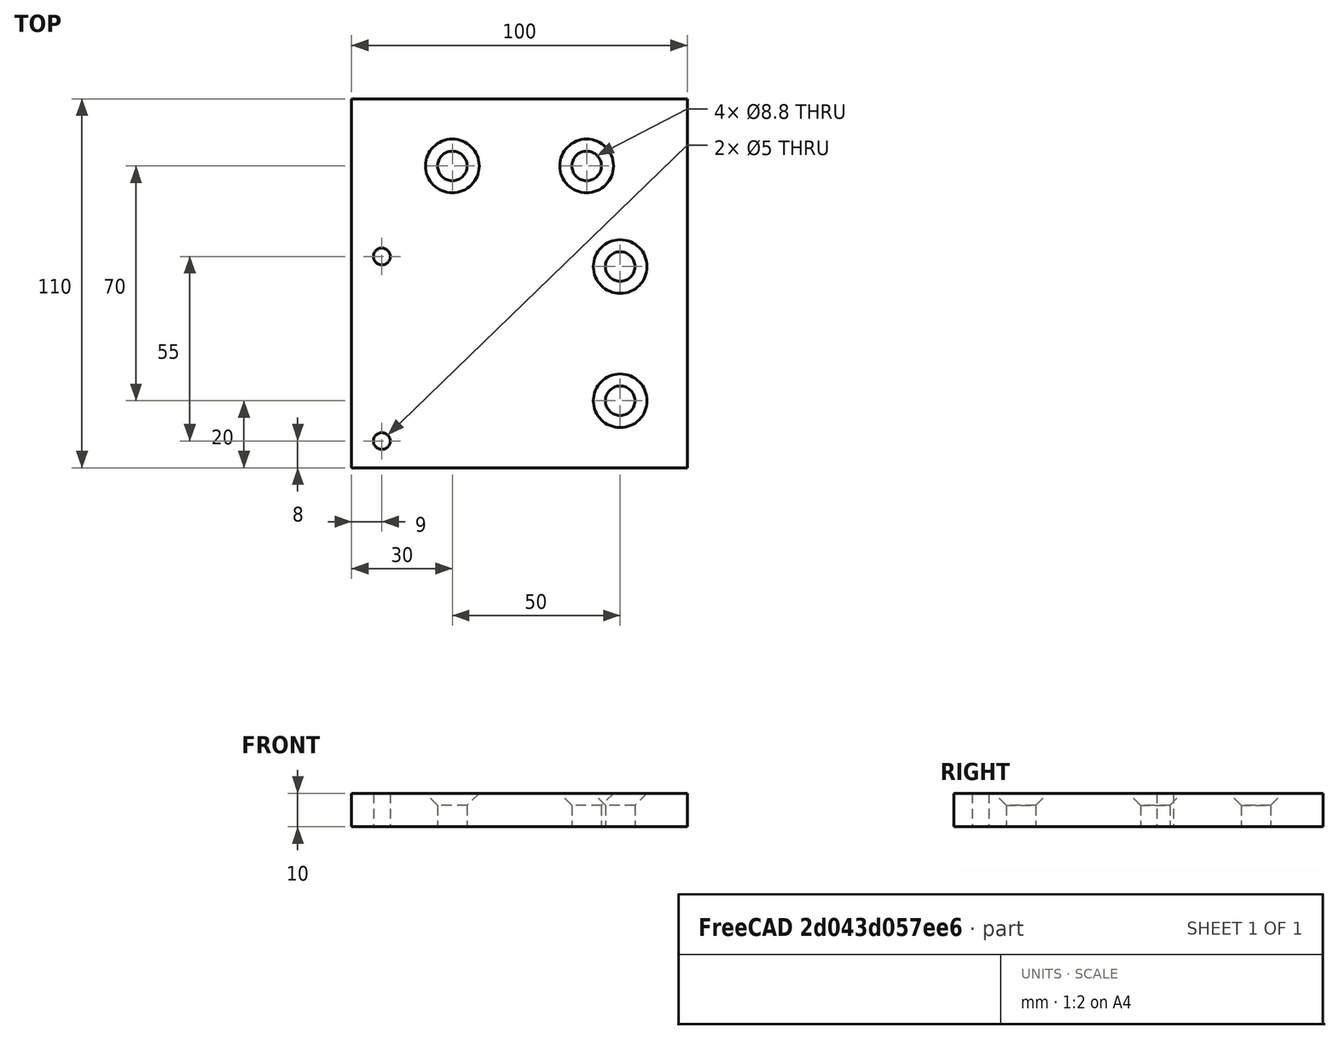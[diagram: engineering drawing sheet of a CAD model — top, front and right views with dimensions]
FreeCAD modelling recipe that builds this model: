
FCSTD DOCUMENT  (FreeCAD 0.17R13528 (Git))
Label: plate3
License: All rights reserved
LicenseURL: http://en.wikipedia.org/wiki/All_rights_reserved
objects: TechDraw::DrawViewDimension×17, Sketcher::SketchObject×4, PartDesign::Hole×3, PartDesign::LinearPattern×3, TechDraw::DrawProjGroupItem×3, PartDesign::Pad×1, PartDesign::Body×1, TechDraw::DrawSVGTemplate×1, TechDraw::DrawProjGroup×1, TechDraw::DrawViewAnnotation×1, TechDraw::DrawPage×1
note: 16 computed .brp shape members not serialized (recipe doc carries the construction recipe); baked Part::Feature solids carry a one-line shape summary decoded from their .brp

FEATURE [Sketcher::SketchObject] Sketch
  MapMode = 5
  Support = -> [XY_Plane]
  sketch-geometry (4):
    g0: LineSegment StartX=0 StartY=0 StartZ=0 EndX=100 EndY=0 EndZ=0
    g1: LineSegment StartX=100 StartY=0 StartZ=0 EndX=100 EndY=110 EndZ=0
    g2: LineSegment StartX=100 StartY=110 StartZ=0 EndX=0 EndY=110 EndZ=0
    g3: LineSegment StartX=0 StartY=110 StartZ=0 EndX=0 EndY=0 EndZ=0
  constraints (11):
    c: Coincident(g0,g1)
    c: Coincident(g1,g2)
    c: Coincident(g2,g3)
    c: Coincident(g3,g0)
    c: Horizontal(g0)
    c: Horizontal(g2)
    c: Vertical(g1)
    c: Vertical(g3)
    c: Coincident(g0,g-1)
    c: DistanceX(g0,g0) = 100
    c: DistanceY(g3,g3) = 110
FEATURE [PartDesign::Pad] Pad
  Length = 10
  Length2 = 100
  Profile = -> Sketch
  Type = 0
FEATURE [Sketcher::SketchObject] Sketch001
  MapMode = 5
  Placement = pos=(0,0,10) rot=(0,0,1;0rad)
  Support = -> [Pad]
  sketch-geometry (1):
    g0: Circle CenterX=9 CenterY=8 CenterZ=0 NormalX=0 NormalY=0 NormalZ=1 AngleXU=0 Radius=4.49838
  constraints (2):
    c: Distance(g0,g-1) = 8
    c: Distance(g0,g-2) = 9
FEATURE [PartDesign::Hole] Hole
  BaseFeature = -> Pad
  Depth = 25
  DepthType = 1
  Diameter = 5
  DrillPoint = 0
  DrillPointAngle = 118
  HoleCutCountersinkAngle = 90
  HoleCutDepth = 0
  HoleCutDiameter = 6
  HoleCutType = 0
  ModelActualThread = false
  Profile = -> Sketch001
  Tapered = false
  TaperedAngle = 90
  ThreadAngle = 60
  ThreadClass = 0
  ThreadCutOffInner = 0.108253
  ThreadCutOffOuter = 0.216506
  ThreadDirection = 1
  ThreadFit = 0
  ThreadPitch = 1
  ThreadSize = 7
  ThreadType = 1
  Threaded = true
FEATURE [PartDesign::LinearPattern] LinearPattern
  BaseFeature = -> Hole
  Direction = -> Sketch001 [V_Axis]
  Length = 55
  Occurrences = 2
  Originals = -> [Hole]
FEATURE [Sketcher::SketchObject] Sketch002
  MapMode = 5
  Placement = pos=(0,0,10) rot=(0,0,1;0rad)
  Support = -> [LinearPattern]
  sketch-geometry (1):
    g0: Circle CenterX=80 CenterY=20 CenterZ=0 NormalX=0 NormalY=0 NormalZ=1 AngleXU=0 Radius=6.26403
  constraints (2):
    c: Distance(g0,g-2) = 80
    c: Distance(g0,g-1) = 20
FEATURE [PartDesign::Hole] Hole001
  BaseFeature = -> LinearPattern
  Depth = 25
  DepthType = 1
  Diameter = 8.8
  DrillPoint = 0
  DrillPointAngle = 118
  HoleCutCountersinkAngle = 90
  HoleCutDepth = 0
  HoleCutDiameter = 16
  HoleCutType = 2
  ModelActualThread = false
  Profile = -> Sketch002
  Tapered = false
  TaperedAngle = 90
  ThreadAngle = 0
  ThreadClass = 0
  ThreadCutOffInner = 0
  ThreadCutOffOuter = 0
  ThreadDirection = 0
  ThreadFit = 0
  ThreadPitch = 0
  ThreadSize = 8
  ThreadType = 1
  Threaded = false
FEATURE [PartDesign::LinearPattern] LinearPattern001
  BaseFeature = -> Hole001
  Direction = -> Sketch002 [V_Axis]
  Length = 40
  Occurrences = 2
  Originals = -> [Hole001]
FEATURE [Sketcher::SketchObject] Sketch003
  MapMode = 5
  Placement = pos=(0,0,10) rot=(0,0,1;0rad)
  Support = -> [LinearPattern001]
  sketch-geometry (1):
    g0: Circle CenterX=30 CenterY=90 CenterZ=0 NormalX=0 NormalY=0 NormalZ=1 AngleXU=0 Radius=7.37034
  constraints (2):
    c: Distance(g0,g-2) = 30
    c: Distance(g0,g-1) = 90
FEATURE [PartDesign::Hole] Hole002
  BaseFeature = -> LinearPattern001
  Depth = 25
  DepthType = 1
  Diameter = 8.8
  DrillPoint = 0
  DrillPointAngle = 118
  HoleCutCountersinkAngle = 90
  HoleCutDepth = 0
  HoleCutDiameter = 16
  HoleCutType = 2
  ModelActualThread = false
  Profile = -> Sketch003
  Tapered = false
  TaperedAngle = 90
  ThreadAngle = 0
  ThreadClass = 0
  ThreadCutOffInner = 0
  ThreadCutOffOuter = 0
  ThreadDirection = 0
  ThreadFit = 0
  ThreadPitch = 0
  ThreadSize = 8
  ThreadType = 1
  Threaded = false
FEATURE [PartDesign::LinearPattern] LinearPattern002
  BaseFeature = -> Hole002
  Direction = -> Sketch003 [H_Axis]
  Length = 40
  Occurrences = 2
  Originals = -> [Hole002]
FEATURE [PartDesign::Body] Body
  Group = -> [Sketch,Pad,Sketch001,Hole,LinearPattern,Sketch002,Hole001,LinearPattern001,Sketch003,Hole002,LinearPattern002]
  Origin = -> Origin
  Tip = -> LinearPattern002
FEATURE [TechDraw::DrawSVGTemplate] Template
  EditableTexts = Designed_by_Name=Lukas Winter; FC-Date=27.08.2018; FC-SC=1:1; FC-SH=1/1; FC-Title=COSI Measure v1.0; Subtitle=Mechanical assembly - plate 3
  Height = 210
  Orientation = 1
  Width = 297
FEATURE [TechDraw::DrawProjGroupItem] ProjItem  label="Front"
  CoarseView = false
  Direction = (0,-1,0)
  Focus = 100
  HardHidden = false
  IsoCount = 0
  IsoHidden = false
  IsoVisible = false
  LockPosition = false
  Perspective = false
  Rotation = 0
  RotationVector = (1,0,0)
  ScaleType = 0
  SeamHidden = false
  SeamVisible = false
  SmoothHidden = false
  SmoothVisible = false
  Source = -> [Body]
  Type = 0
  X = -65
  Y = 0
FEATURE [TechDraw::DrawProjGroupItem] ProjItem001  label="Left"
  CoarseView = false
  Direction = (-1,0,0)
  Focus = 100
  HardHidden = false
  IsoCount = 0
  IsoHidden = false
  IsoVisible = false
  LockPosition = false
  Perspective = false
  Rotation = 0
  RotationVector = (0,1,0)
  ScaleType = 0
  SeamHidden = false
  SeamVisible = false
  SmoothHidden = false
  SmoothVisible = false
  Source = -> [Body]
  Type = 1
  X = 125
  Y = 0
FEATURE [TechDraw::DrawProjGroupItem] ProjItem002  label="Top"
  CoarseView = false
  Direction = (0,0,1)
  Focus = 100
  HardHidden = false
  IsoCount = 0
  IsoHidden = false
  IsoVisible = false
  LockPosition = false
  Perspective = false
  Rotation = 0
  RotationVector = (1,0,0)
  ScaleType = 0
  SeamHidden = false
  SeamVisible = false
  SmoothHidden = false
  SmoothVisible = false
  Source = -> [Body]
  Type = 4
  X = 0
  Y = -82.7024
FEATURE [TechDraw::DrawProjGroup] ProjGroup
  Anchor = -> ProjItem
  AutoDistribute = true
  CubeDirs = (1) [(0,0,0)]
  CubeRotations = (1) [(0,0,0)]
  LockPosition = false
  ProjectionType = 0
  Rotation = 0
  ScaleType = 0
  Source = -> [Body]
  Views = -> [ProjItem,ProjItem001,ProjItem002]
  X = 73.7469
  Y = 170.247
  spacingX = 15
  spacingY = 15
FEATURE [TechDraw::DrawViewDimension] Dimension
  FormatSpec = %.2f
  LockPosition = false
  MeasureType = 1
  References2D = -> [ProjItem]
  Rotation = 0
  ScaleType = 0
  Type = 1
  X = 1.72839
  Y = 17.9321
FEATURE [TechDraw::DrawViewDimension] Dimension001
  FormatSpec = %.2f
  LockPosition = false
  MeasureType = 1
  References2D = -> [ProjItem001]
  Rotation = 0
  ScaleType = 0
  Type = 1
  X = -0.432099
  Y = 18.1481
FEATURE [TechDraw::DrawViewDimension] Dimension002
  FormatSpec = %.2f
  LockPosition = false
  MeasureType = 1
  References2D = -> [ProjItem001]
  Rotation = 0
  ScaleType = 0
  Type = 2
  X = 67.8395
  Y = -15.5556
FEATURE [TechDraw::DrawViewDimension] Dimension009
  FormatSpec = %.2f
  LockPosition = false
  MeasureType = 1
  References2D = -> [ProjItem002]
  Rotation = 0
  ScaleType = 0
  Type = 1
  X = -38.3704
  Y = -65.5926
FEATURE [TechDraw::DrawViewDimension] Dimension010
  FormatSpec = %.2f
  LockPosition = false
  MeasureType = 1
  References2D = -> [ProjItem002]
  Rotation = 0
  ScaleType = 0
  Type = 2
  X = -34.8405
  Y = -38.7919
FEATURE [TechDraw::DrawViewDimension] Dimension015
  FormatSpec = %.2f
  LockPosition = false
  MeasureType = 1
  References2D = -> [ProjItem002]
  Rotation = 0
  ScaleType = 0
  Type = 2
  X = 9.07407
  Y = 52.6296
FEATURE [TechDraw::DrawViewAnnotation] Annotation
  Font = osifont
  LineSpace = 80
  LockPosition = false
  MaxWidth = -1
  Rotation = 0
  ScaleType = 0
  Text = Make a M6 thread in the d=5mm holes. | Make a countersink in the d=8.8mm holes.
  TextSize = 4
  TextStyle = 0
  X = 235.04
  Y = 73.6414
FEATURE [TechDraw::DrawViewDimension] Dimension019
  FormatSpec = %.2f
  LockPosition = false
  MeasureType = 1
  References2D = -> [ProjItem002]
  Rotation = 0
  ScaleType = 0
  Type = 2
  X = -44.4854
  Y = -19.2041
FEATURE [TechDraw::DrawViewDimension] Dimension020
  FormatSpec = %.2f
  LockPosition = false
  MeasureType = 1
  References2D = -> [ProjItem002]
  Rotation = 0
  ScaleType = 0
  Type = 1
  X = 0.972358
  Y = 38.6512
FEATURE [TechDraw::DrawViewDimension] Dimension021
  FormatSpec = %.2f
  LockPosition = false
  MeasureType = 1
  References2D = -> [ProjItem002]
  Rotation = 0
  ScaleType = 0
  Type = 1
  X = -34.7618
  Y = 38.6512
FEATURE [TechDraw::DrawViewDimension] Dimension022
  FormatSpec = %.2f
  LockPosition = false
  MeasureType = 1
  References2D = -> [ProjItem002]
  Rotation = 0
  ScaleType = 0
  Type = 1
  X = 39.1374
  Y = 38.6512
FEATURE [TechDraw::DrawViewDimension] Dimension023
  FormatSpec = %.2f
  LockPosition = false
  MeasureType = 1
  References2D = -> [ProjItem002]
  Rotation = 0
  ScaleType = 0
  Type = 5
  X = -1.70163
  Y = -18.2317
FEATURE [TechDraw::DrawViewDimension] Dimension024
  FormatSpec = %.2f
  LockPosition = false
  MeasureType = 1
  References2D = -> [ProjItem002]
  Rotation = 0
  ScaleType = 0
  Type = 5
  X = -1.70163
  Y = -18.2317
FEATURE [TechDraw::DrawViewDimension] Dimension025
  FormatSpec = %.2f
  LockPosition = false
  MeasureType = 1
  References2D = -> [ProjItem002]
  Rotation = 0
  ScaleType = 0
  Type = 5
  X = -17.0163
  Y = 17.9886
FEATURE [TechDraw::DrawViewDimension] Dimension026
  FormatSpec = %.2f
  LockPosition = false
  MeasureType = 1
  References2D = -> [ProjItem002]
  Rotation = 0
  ScaleType = 0
  Type = 5
  X = -8.02196
  Y = 22.6073
FEATURE [TechDraw::DrawViewDimension] Dimension027
  FormatSpec = %.2f
  LockPosition = false
  MeasureType = 1
  References2D = -> [ProjItem002]
  Rotation = 0
  ScaleType = 0
  Type = 2
  X = 26.4968
  Y = -45.2147
FEATURE [TechDraw::DrawViewDimension] Dimension028
  FormatSpec = %.2f
  LockPosition = false
  MeasureType = 1
  References2D = -> [ProjItem002]
  Rotation = 0
  ScaleType = 0
  Type = 2
  X = 26.2537
  Y = -14.8285
FEATURE [TechDraw::DrawViewDimension] Dimension029
  FormatSpec = %.2f
  LockPosition = false
  MeasureType = 1
  References2D = -> [ProjItem002]
  Rotation = 0
  ScaleType = 0
  Type = 1
  X = 39.8667
  Y = -5.83415
FEATURE [TechDraw::DrawPage] Page
  KeepUpdated = true
  ProjectionType = 0
  Template = -> Template
  Views = -> [ProjGroup,Dimension,Dimension001,Dimension002,Dimension009,Dimension010,Dimension015,Annotation,Dimension019,Dimension020,Dimension021,Dimension022,Dimension023,Dimension024,Dimension025,Dimension026,Dimension027,Dimension028,Dimension029]
